# Revit family: DO_WPB_Dynamicroll-Food-Inox_BMP
name_source: partatom
category: Doors
units: mm (PartAtom-declared; Revit-internal decimal feet)

## family parameters
Always vertical = Yes
Cut with Voids When Loaded = Yes
OmniClass Number = 23.17.11.45.17
Room Calculation Point = No
Shared = No
Work Plane-Based = Yes

## types (1)
- Dynamicroll Food Inox
    Analytic Construction = <None>
    Classification.OmniClass.23.Description = Rapid Opening Doors
    Classification.OmniClass.23.Number = 23.17.11.45.17
    Classification.Uniclass.EF.Description = Doors
    Classification.Uniclass.EF.Number = EF_25_30_25
    Classification.Uniclass.Pr.Description = High-speed doorsets
    Classification.Uniclass.Pr.Number = Pr_30_59_24_38
    Classification.Uniclass.Ss.Description = High-speed doorset systems
    Classification.Uniclass.Ss.Number = Ss_25_30_20_38
    Default Elevation = 0 mm  [stored 0 ft]
    Define Thermal Properties by = Schematic Type
    Description = High Speed Door
    IfcDescription = High Speed Door
    IfcExportAs = IfcDoor
    IfcExportType = DOOR
    LOD300 = No
    LOD400 = Yes
    Manufacturer = BMP High Speed Doors
    Model = Dynamicroll Food Inox
    RSen_C_clashvolume = No
    RSen_C_code_ETIM = EC003229
    RSen_C_code_ETIM_url = https://prod.etim-international.com
    RSen_C_content_modification_date = 2025.01.22
    RSen_C_content_provider = BMP High Speed Doors
    RSen_C_content_version = V2
    RSen_C_model = Dynamicroll Food Inox
    csv = Dynamicroll
    csv_metadata = Dynamicroll_data
    curtain_bottom_height = 120 mm  [stored 0.393701 ft]
    curtain_bottom_material = Plastic, black
    curtain_material = PVC
    do_type0 = curtain : panel
    do_type1 = curtain : rectangle window
    do_type2 = curtain : full width window
    do_type3 = curtain : full vision window
    do_type4 = curtain : rounded corner window
    ee_type1 = EE_WPB_control panel_BMP_SH : Control panel SS304
    ee_type2 = EE_WPB_control panel_BMP_SH : Control panel PVC
    ee_type3 = EE_WPB_control panel_BMP_SH : Control panel One
    ee_type4 = EE_WPB_control panel_BMP_SH : Control panel Powder coated steel
    frame_material = Steel, stainless 304
    motor_cover_material = Steel, stainless 304
    region_index = 44
    si_type0 = window type : No windows
    si_type1 = window type : Rectangle window
    si_type2 = window type : Full width window
    si_type3 = window type : Full vision window
    si_type4 = window type : Rounded corner window
    si_type5 = curtain type : Standard curtain
    si_type6 = curtain type : Insulated curtain 7mm
    si_type7 = curtain type : FDA approved curtain
    si_type8 = curtain type : Antistatic curtain
    si_type9 = curtain type : Translucent curtain
    type_index = 5
    window_material = Glass, transparent

note: [stored X ft] marks values corroborated as IEEE doubles in the binary element streams (Revit-internal decimal feet)

## geometry (parser evidence)
native form markers: Sweep x33
no freeform markers — native parametric forms only
